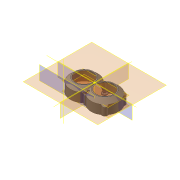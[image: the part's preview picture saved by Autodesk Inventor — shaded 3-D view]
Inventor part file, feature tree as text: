
AUTODESK INVENTOR PART (.ipt)
format: ipt  version: 2015 SP2 (Build 190223200, 223)  size: 468,480 bytes
history: native  units: mm
features: sketch x24, extrude x16, projected_geometry x8, plane x6, fillet x4, loft x3, reference x2, other x1, shell x1, chamfer x1, mirror x1
ambient origin geometry x8: Origin, YZ Plane, XZ Plane, XY Plane, X Axis, Y Axis, Z Axis, Center Point
bodies: Body1 (feature_tree)
feature tree (67):
  other  "Sólido1"
  sketch  "Boceto1"  dims[d0=31.0mm d1=31.0mm]
  plane  "Plano de trabajo1"
  sketch  "Boceto2"  dims[d2=1.6mm d3=1.6mm]
  plane  "Plano de trabajo2"
  loft  "Solevación1"
  loft  "Solevación2"
  loft  "Solevación3"
  extrude  "Extrusión2"  Depth=1.6mm
  plane  "Plano de trabajo6"
  plane  "Plano de trabajo3"
  extrude  "Extrusión6"  Depth=1.6mm
  plane  "Plano de trabajo5"
  extrude  "Extrusión7"  TaperAngle=0.0deg  [1 undecoded]
  shell  "Vaciado2"  Thickness=0.0mm
  extrude  "Extrusión8"  TaperAngle=0.0deg  [1 undecoded]
  extrude  "Extrusión12"  Depth=1.6mm
  extrude  "Extrusión13"  TaperAngle=0.0deg  [1 undecoded]
  extrude  "Extrusión14"  Depth=9.19mm
  extrude  "Extrusión15"  [1 undecoded]
  sketch  "Boceto21"  dims[d64=37.0mm d65=9.0mm]
  fillet  "Empalme1"  Radius=5.0mm
  sketch  "Boceto22"  dims[d66=4.0mm d67=1.6mm d68=0.0mm]
  extrude  "Extrusión18"  Depth=15.0mm TaperAngle=0.0deg
  extrude  "Extrusión19"  Depth=5.0mm
  extrude  "Extrusión20"  Depth=10.0mm
  fillet  "Empalme2"  Radius=37.0mm
  extrude  "Extrusión21"  Depth=9.0mm
  sketch  "Boceto26"  dims[d89=10.0mm d90=0.0mm d91=7.0mm d97=1.0mm]
  extrude  "Extrusión22"  Depth=1.6mm TaperAngle=0.0deg
  chamfer  "Chaflán1"  Distance=1.6mm
  extrude  "Extrusión23"  Depth=1.6mm TaperAngle=0.0deg
  mirror  "Simetría1"
  extrude  "Extrusión24"  Depth=1.6mm TaperAngle=0.0deg
  fillet  "Empalme4"  Radius=6.0mm
  extrude  "Extrusión25"  Depth=10.0mm
  fillet  "Empalme3"  Radius=1.0mm
  sketch  "Boceto3"  dims[d5=-22.6mm d6=48.6mm]
  sketch  "Boceto4"  dims[d7=48.6mm d8=1.6mm]
  projected_geometry  "Contorno proyectado1"
  sketch  "Boceto5"  dims[d9=1.6mm d11=18.579131mm]
  projected_geometry  "Contorno proyectado2"
  sketch  "Boceto6"  dims[d12=16.0mm d13=0.0mm d14=90.0deg d15=0.0mm d16=90.0deg]
  sketch  "Boceto7"  dims[d17=0.0mm d18=90.0deg d19=0.0mm d20=90.0deg]
  sketch  "Boceto11"  dims[d21=31.0mm d22=1.6mm]
  plane  "Plano de trabajo4"
  sketch  "Boceto12"  dims[d23=48.6mm d24=0.0mm d25=90.0deg]
  sketch  "Boceto13"  dims[d26=0.0mm d27=90.0deg d29=9.19mm]
  reference  "Referencia1"
  sketch  "Boceto16"  dims[d33=1.58mm d34=0.0mm d43=-20.25mm d44=5.0mm]
  sketch  "Boceto17"  dims[d45=3.0mm d46=15.0mm d47=0.0mm]
  sketch  "Boceto19"  dims[d48=-7.853982mm d49=-39.0mm d50=5.0mm]
  projected_geometry  "Contorno proyectado4"
  sketch  "Boceto20"  dims[d51=10.0mm d52=0.0mm d62=1.0mm d63=37.0mm]
  reference  "Referencia2"
  projected_geometry  "Contorno proyectado5"
  projected_geometry  "Contorno proyectado6"
  sketch  "Boceto23"  dims[d76=4.0mm d77=1.6mm d78=0.0mm]
  projected_geometry  "Contorno proyectado7"
  sketch  "Boceto24"  dims[d79=6.0mm d80=1.6mm d81=0.0mm]
  sketch  "Boceto25"  dims[d84=3.0mm d85=1.6mm d86=0.0mm d87=6.0mm]
  projected_geometry  "Contorno proyectado8"
  sketch  "Boceto27"  dims[d98=31.0mm]
  projected_geometry  "Contorno proyectado9"
  sketch  "Boceto28"  dims[d101=31.0mm]
  sketch  "Boceto29"  dims[d102=15.744556mm]
  sketch  "Boceto30"  dims[d103=15.745mm d104=10.0mm d105=0.0mm d106=1.6mm d107=7.0mm d108=0.0mm d109=1.6mm d110=0.0mm d111=0.0mm d112=1.0mm d113=3.0mm d114=0.0mm d115=2.9mm d116=3.0mm d117=0.0mm d118=2.0mm d119=2.0mm d120=45.0deg d121=7.0mm d122=31.3mm d123=31.3mm d124=5.0mm d125=0.0mm d126=8.0mm d127=0.0mm d128=2.0mm d129=4.0mm d130=9.0mm d131=1.6mm d132=0.0mm]
note: 4 required parameter values undecoded (feature->parameter linkage not recoverable at this tier; creation-order binding heuristic only, values carry confidence <= 0.55)
